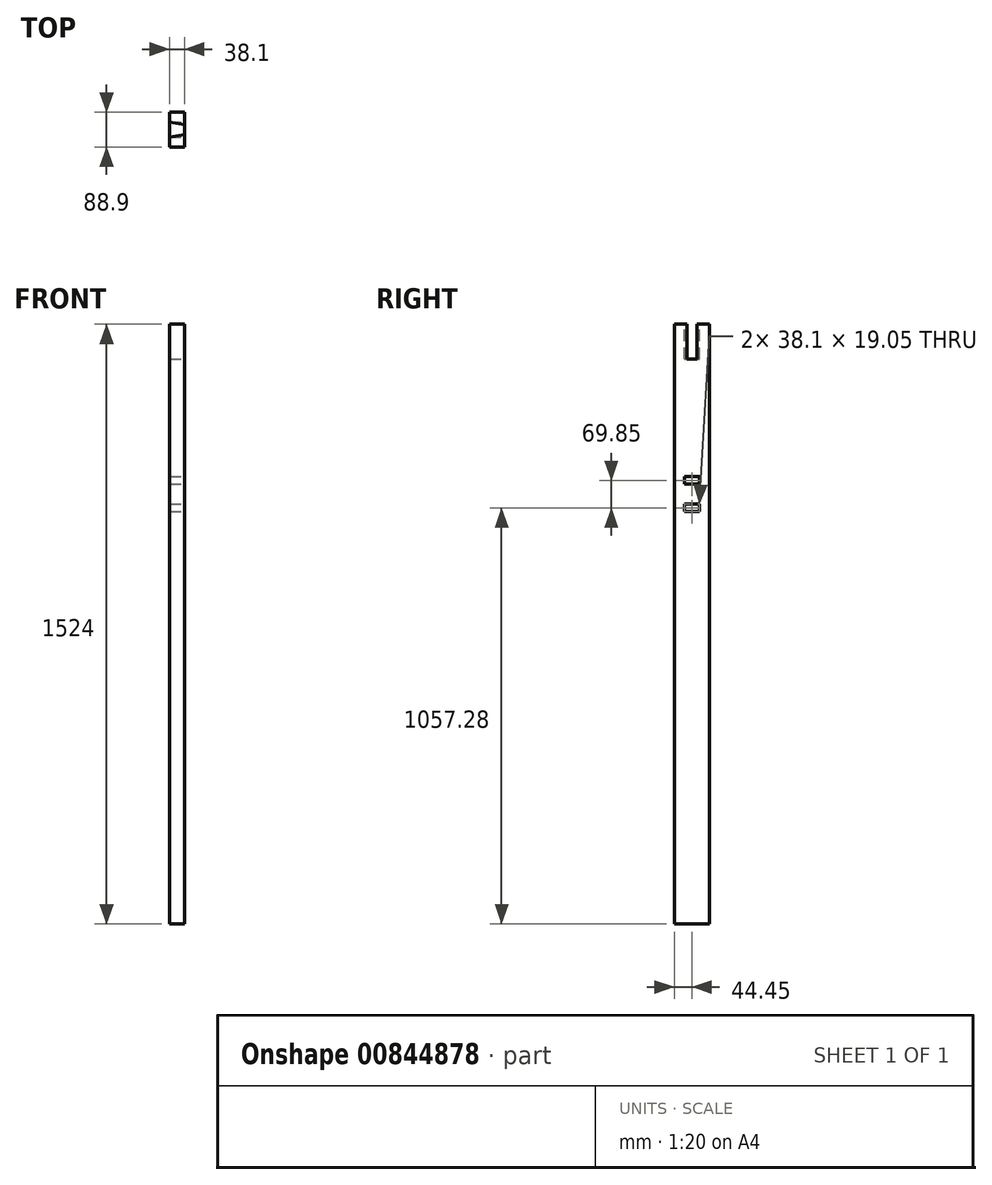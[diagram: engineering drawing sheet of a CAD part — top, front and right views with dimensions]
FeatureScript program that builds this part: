
annotation { "Feature Type Name" : "Feature", "Feature Type Description" : "" }
export const myFeature = defineFeature(function(context is Context, id is Id, definition is map)
    precondition{}
    {
        {
            var Q0;
            Q0=qCreatedBy(makeId("Top.planeOp"),FACE);
            var sketch = newSketch(context, id + "F0", { "sketchPlane" : qUnion([Q0])});
            skLineSegment(sketch, "E0.bottom", {"start": v(0, 0) * mm, "end": v(38.1, 0) * mm});
            skLineSegment(sketch, "E0.top", {"start": v(0, 88.9) * mm, "end": v(38.1, 88.9) * mm});
            skLineSegment(sketch, "E0.left", {"start": v(0, 0) * mm, "end": v(0, 88.9) * mm});
            skLineSegment(sketch, "E0.right", {"start": v(38.1, 0) * mm, "end": v(38.1, 88.9) * mm});
            skSolve(sketch);
        }
        {
            var Q0;
            Q0=makeQuery(id+"F0.imprint","IMPRINT",FACE,{"disambiguationData":[TD([[makeQuery(id+"F0.imprint","IMPRINT",EDGE,{"derivedFrom":sQuery(id+"F0.wireOp",EDGE,"E0.bottom")}),1.0]])]});
            extrude(context, id + "F1", {"entities" : qUnion([Q0]), "depth" : 1524 * mm, "offsetDistance" : 25.4 * mm});
        }
        {
            var Q0;
            Q0=makeQuery(id+"F1.opExtrude","SWEPT_FACE",FACE,{"disambiguationData":[OSD([sQuery(id+"F0.wireOp",EDGE,"E0.right")])]});
            var sketch = newSketch(context, id + "F2", { "sketchPlane" : qUnion([Q0])});
            skLineSegment(sketch, "E1.bottom", {"start": v(25.4, 1136.65) * mm, "end": v(63.5, 1136.65) * mm});
            skLineSegment(sketch, "E1.top", {"start": v(25.4, 1117.6) * mm, "end": v(63.5, 1117.6) * mm});
            skLineSegment(sketch, "E1.left", {"start": v(25.4, 1136.65) * mm, "end": v(25.4, 1117.6) * mm});
            skLineSegment(sketch, "E1.right", {"start": v(63.5, 1136.65) * mm, "end": v(63.5, 1117.6) * mm});
            skLineSegment(sketch, "E2.bottom", {"start": v(25.4, 1066.8) * mm, "end": v(63.5, 1066.8) * mm});
            skLineSegment(sketch, "E2.top", {"start": v(25.4, 1047.75) * mm, "end": v(63.5, 1047.75) * mm});
            skLineSegment(sketch, "E2.left", {"start": v(25.4, 1066.8) * mm, "end": v(25.4, 1047.75) * mm});
            skLineSegment(sketch, "E2.right", {"start": v(63.5, 1066.8) * mm, "end": v(63.5, 1047.75) * mm});
            skSolve(sketch);
        }
        {
            var Q0;
            Q0=makeQuery(id+"F2.imprint","IMPRINT",FACE,{"disambiguationData":[TD([[makeQuery(id+"F2.imprint","IMPRINT",EDGE,{"derivedFrom":sQuery(id+"F2.wireOp",EDGE,"E1.bottom")}),-1.0]])]});
            var Q1;
            Q1=makeQuery(id+"F2.imprint","IMPRINT",FACE,{"disambiguationData":[TD([[makeQuery(id+"F2.imprint","IMPRINT",EDGE,{"derivedFrom":sQuery(id+"F2.wireOp",EDGE,"E2.bottom")}),-1.0]])]});
            extrude(context, id + "F3", {"entities" : qUnion([Q0, Q1]), "operationType" : NewBodyOperationType.REMOVE, "endBound" : BoundingType.UP_TO_NEXT, "oppositeDirection" : true, "depth" : 25.4 * mm, "offsetDistance" : 25.4 * mm});
        }
        {
            var Q0;
            Q0=makeQuery(id+"F1.opExtrude","CAP_FACE",FACE,{"disambiguationData":[OSD([sQuery(id+"F0.wireOp",EDGE,"E0.bottom"),sQuery(id+"F0.wireOp",EDGE,"E0.top"),sQuery(id+"F0.wireOp",EDGE,"E0.left"),sQuery(id+"F0.wireOp",EDGE,"E0.right")])],"isStart":false});
            var sketch = newSketch(context, id + "F4", { "sketchPlane" : qUnion([Q0])});
            skLineSegment(sketch, "E3", {"start": v(0, 25.4) * mm, "end": v(38.1, 31.75) * mm});
            skLineSegment(sketch, "E4", {"start": v(38.1, 31.75) * mm, "end": v(38.1, 57.15) * mm});
            skLineSegment(sketch, "E5", {"start": v(38.1, 57.15) * mm, "end": v(0, 63.5) * mm});
            skLineSegment(sketch, "E6", {"start": v(0, 63.5) * mm, "end": v(0, 25.4) * mm});
            skSolve(sketch);
        }
        {
            var Q0;
            Q0=makeQuery(id+"F4.imprint","IMPRINT",FACE,{"disambiguationData":[TD([[makeQuery(id+"F4.imprint","IMPRINT",EDGE,{"derivedFrom":sQuery(id+"F4.wireOp",EDGE,"E3")}),1.0]])]});
            extrude(context, id + "F5", {"entities" : qUnion([Q0]), "operationType" : NewBodyOperationType.REMOVE, "oppositeDirection" : true, "depth" : 88.9 * mm, "offsetDistance" : 25.4 * mm});
        }
    });
